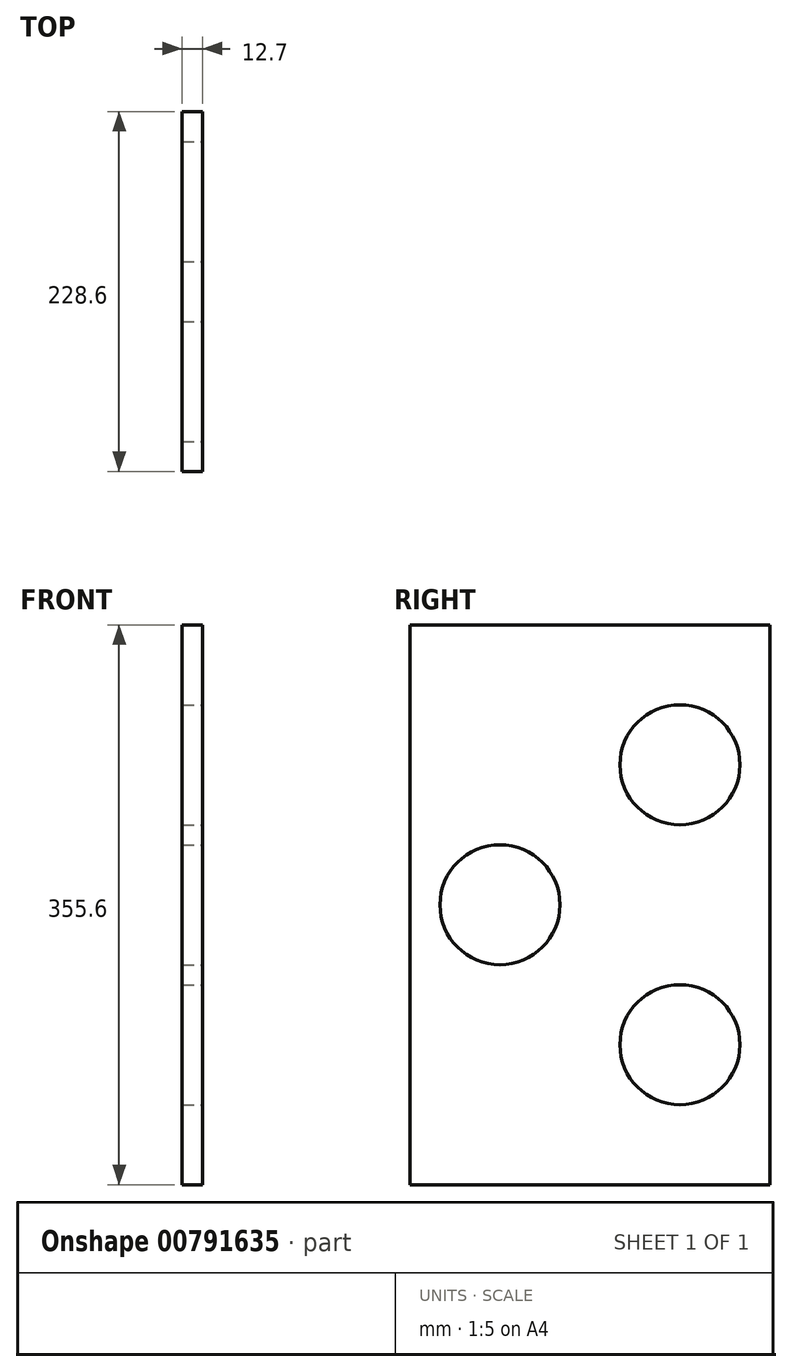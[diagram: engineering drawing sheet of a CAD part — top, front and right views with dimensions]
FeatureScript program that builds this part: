
annotation { "Feature Type Name" : "Feature", "Feature Type Description" : "" }
export const myFeature = defineFeature(function(context is Context, id is Id, definition is map)
    precondition{}
    {
        {
            var Q0;
            Q0=qCreatedBy(makeId("Right.planeOp"),FACE);
            var sketch = newSketch(context, id + "F0", { "sketchPlane" : qUnion([Q0])});
            skLineSegment(sketch, "E0.bottom", {"start": v(-114.3, 177.8) * mm, "end": v(114.3, 177.8) * mm});
            skLineSegment(sketch, "E0.top", {"start": v(-114.3, -177.8) * mm, "end": v(114.3, -177.8) * mm});
            skLineSegment(sketch, "E0.left", {"start": v(-114.3, 177.8) * mm, "end": v(-114.3, -177.8) * mm});
            skLineSegment(sketch, "E0.right", {"start": v(114.3, 177.8) * mm, "end": v(114.3, -177.8) * mm});
            skPoint(sketch, "E0.middle", {"position": v(0, 0) * mm});
            skSolve(sketch);
        }
        {
            var Q0;
            Q0=makeQuery(id+"F0.imprint","IMPRINT",FACE,{"disambiguationData":[TD([[makeQuery(id+"F0.imprint","IMPRINT",EDGE,{"derivedFrom":sQuery(id+"F0.wireOp",EDGE,"E0.bottom")}),-1.0]])]});
            extrude(context, id + "F1", {"entities" : qUnion([Q0]), "depth" : 12.7 * mm, "offsetDistance" : 25.4 * mm});
        }
        {
            var Q0;
            Q0=makeQuery(id+"F1.opExtrude","CAP_FACE",FACE,{"disambiguationData":[OSD([sQuery(id+"F0.wireOp",EDGE,"E0.bottom"),sQuery(id+"F0.wireOp",EDGE,"E0.top"),sQuery(id+"F0.wireOp",EDGE,"E0.left"),sQuery(id+"F0.wireOp",EDGE,"E0.right")])],"isStart":false});
            var sketch = newSketch(context, id + "F2", { "sketchPlane" : qUnion([Q0])});
            skCircle(sketch, "E1", {"center": v(-57.15, 0) * mm, "radius": 38.1 * mm});
            skCircle(sketch, "E2", {"center": v(57.15, 88.9) * mm, "radius": 38.1 * mm});
            skCircle(sketch, "E3", {"center": v(57.15, -88.9) * mm, "radius": 38.1 * mm});
            skLineSegment(sketch, "E4", {"start": v(57.15, 88.9) * mm, "end": v(57.15, 177.8) * mm});
            skLineSegment(sketch, "E5", {"start": v(-57.15, 0) * mm, "end": v(-57.15, 177.8) * mm});
            skLineSegment(sketch, "E6", {"start": v(57.15, -88.9) * mm, "end": v(57.15, -177.8) * mm});
            skSolve(sketch);
        }
        {
            var Q0;
            Q0=sQuery(id+"F2.wireOp",VERTEX,"E3.center");
            var Q1;
            Q1=sQuery(id+"F2.wireOp",VERTEX,"E1.center");
            var Q2;
            Q2=sQuery(id+"F2.wireOp",VERTEX,"E2.center");
            var Q3;
            Q3=makeQuery(id+"F1.opExtrude","SWEPT_BODY",BODY,{"disambiguationData":[OSD([sQuery(id+"F0.wireOp",EDGE,"E0.bottom"),sQuery(id+"F0.wireOp",EDGE,"E0.top"),sQuery(id+"F0.wireOp",EDGE,"E0.left"),sQuery(id+"F0.wireOp",EDGE,"E0.right")])]});
            hole(context, id + "F3", {"style" : HoleStyle.SIMPLE, "endStyle" : HoleEndStyle.THROUGH, "holeDiameter" : 76.2 * mm, "majorDiameter" : 6.35 * mm, "isTappedThrough" : true, "tappedDepth" : 12.7 * mm, "tapClearance" : 3, "locations" : qUnion([Q0, Q1, Q2]), "scope" : qUnion([Q3])});
        }
    });
